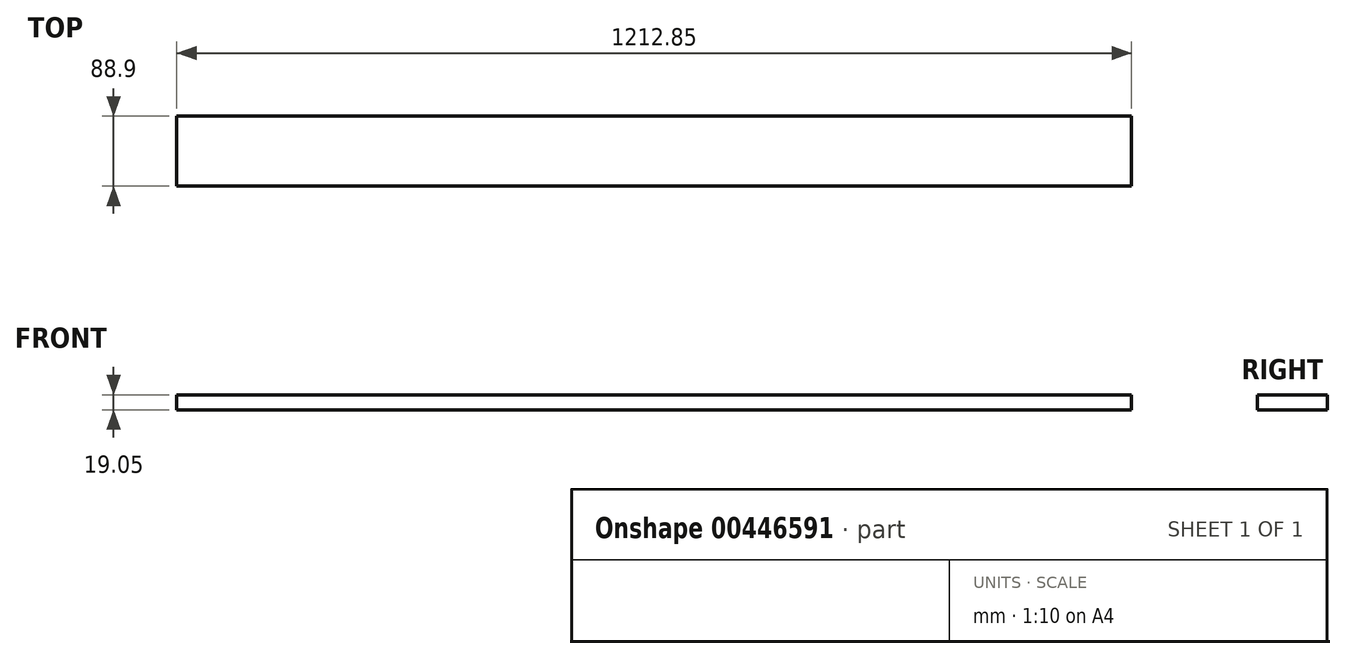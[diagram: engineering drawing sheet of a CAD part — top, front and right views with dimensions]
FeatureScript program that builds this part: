
annotation { "Feature Type Name" : "Feature", "Feature Type Description" : "" }
export const myFeature = defineFeature(function(context is Context, id is Id, definition is map)
    precondition{}
    {
        {
            var Q0;
            Q0=qCreatedBy(makeId("Front.planeOp"),FACE);
            var sketch = newSketch(context, id + "F0", { "sketchPlane" : qUnion([Q0])});
            skLineSegment(sketch, "E0.bottom", {"start": v(0, 0) * mm, "end": v(1212.85, 0) * mm});
            skLineSegment(sketch, "E0.top", {"start": v(0, 2032) * mm, "end": v(1212.85, 2032) * mm});
            skLineSegment(sketch, "E0.left", {"start": v(0, 0) * mm, "end": v(0, 2032) * mm});
            skLineSegment(sketch, "E0.right", {"start": v(1212.85, 0) * mm, "end": v(1212.85, 2032) * mm});
            skLineSegment(sketch, "E1", {"start": v(0, 2012.95) * mm, "end": v(1212.85, 2012.95) * mm});
            skLineSegment(sketch, "E2", {"start": v(0, 19.05) * mm, "end": v(19.05, 19.05) * mm});
            skLineSegment(sketch, "E3", {"start": v(19.05, 2012.95) * mm, "end": v(19.05, 19.05) * mm});
            skLineSegment(sketch, "E4", {"start": v(1193.8, 2012.95) * mm, "end": v(1193.8, 19.05) * mm});
            skLineSegment(sketch, "E5.trimOffspring", {"start": v(1193.8, 19.05) * mm, "end": v(1212.85, 19.05) * mm});
            skLineSegment(sketch, "E6", {"start": v(19.05, 19.05) * mm, "end": v(1193.8, 19.05) * mm});
            skSolve(sketch);
        }
        {
            var Q0;
            {var subQ5=sQuery(id+"F0.wireOp",EDGE,"E0.top");Q0=makeQuery(id+"F0.imprint","IMPRINT",FACE,{"disambiguationData":[TD([[makeQuery(id+"F0.imprint","IMPRINT",EDGE,{"derivedFrom":subQ5}),-1.0]])]});}
            extrude(context, id + "F1", {"entities" : qUnion([Q0]), "oppositeDirection" : true, "depth" : 88.9 * mm});
        }
    });
